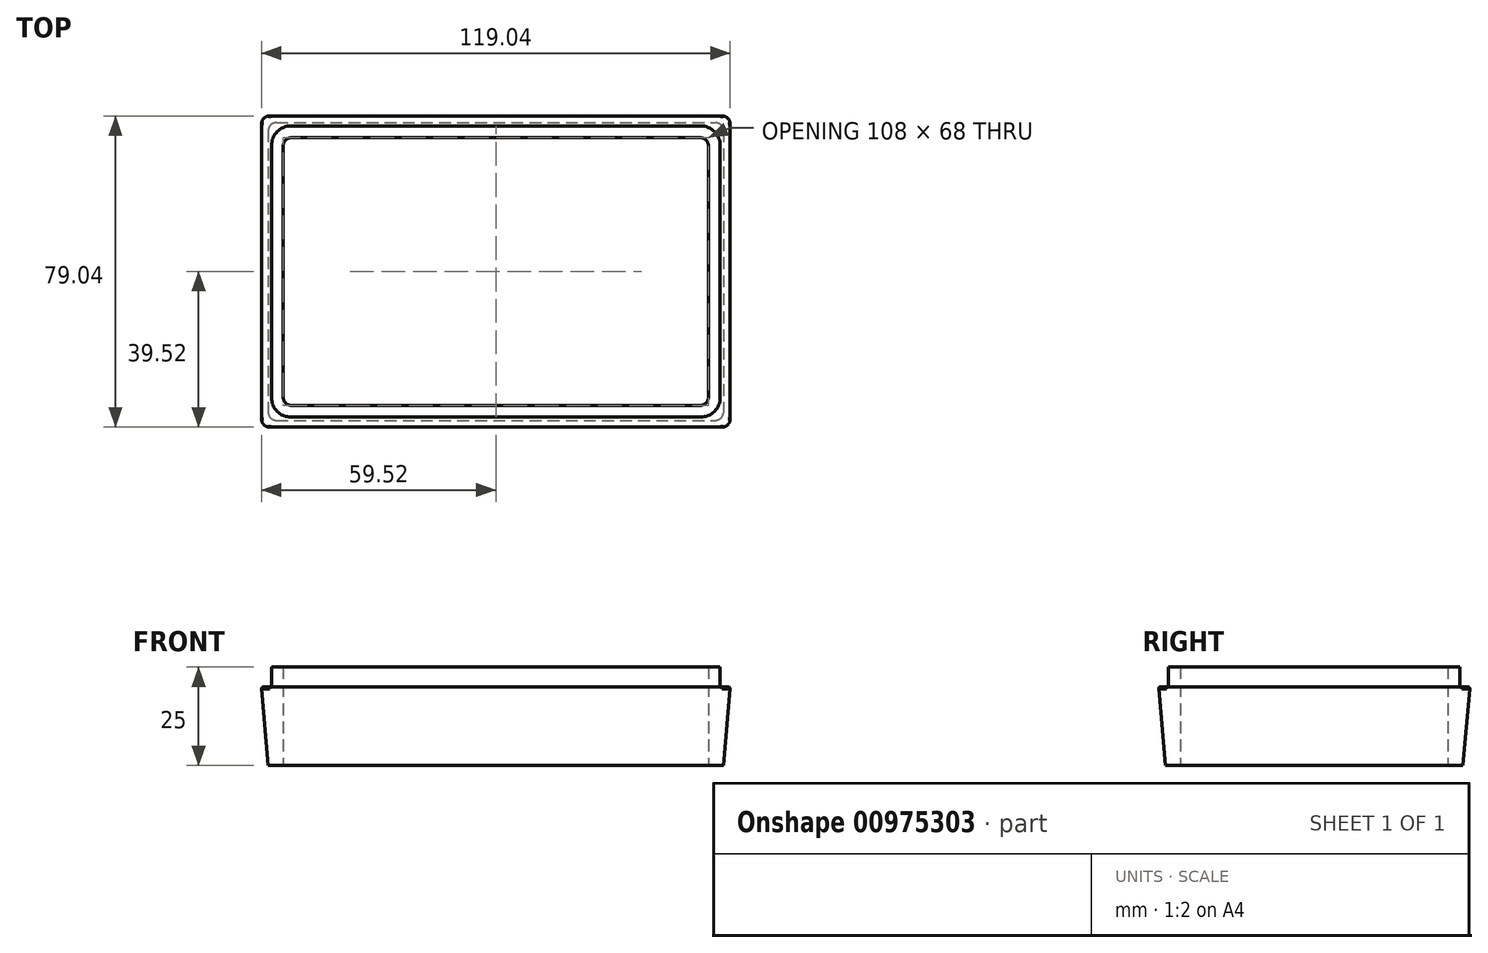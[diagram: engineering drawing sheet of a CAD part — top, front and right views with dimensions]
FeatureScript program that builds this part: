
annotation { "Feature Type Name" : "Feature", "Feature Type Description" : "" }
export const myFeature = defineFeature(function(context is Context, id is Id, definition is map)
    precondition{}
    {
        {
            var Q0;
            Q0=qCreatedBy(makeId("Top.planeOp"),FACE);
            var sketch = newSketch(context, id + "F0", { "sketchPlane" : qUnion([Q0])});
            skLineSegment(sketch, "E0.bottom", {"start": v(-60, 40) * mm, "end": v(60, 40) * mm});
            skLineSegment(sketch, "E0.top", {"start": v(-60, -40) * mm, "end": v(60, -40) * mm});
            skLineSegment(sketch, "E0.left", {"start": v(-60, 40) * mm, "end": v(-60, -40) * mm});
            skLineSegment(sketch, "E0.right", {"start": v(60, 40) * mm, "end": v(60, -40) * mm});
            skLineSegment(sketch, "E1.bottom", {"start": v(-54, 34) * mm, "end": v(54, 34) * mm});
            skLineSegment(sketch, "E1.top", {"start": v(-54, -34) * mm, "end": v(54, -34) * mm});
            skLineSegment(sketch, "E1.left", {"start": v(-54, 34) * mm, "end": v(-54, -34) * mm});
            skLineSegment(sketch, "E1.right", {"start": v(54, 34) * mm, "end": v(54, -34) * mm});
            skSolve(sketch);
        }
        {
            var Q0;
            Q0 = qSketchRegion(id + "F0", true);
            extrude(context, id + "F1", {"entities" : qUnion([Q0]), "depth" : 25 * mm, "offsetDistance" : 25 * mm});
        }
        {
            var Q0;
            Q0=makeQuery(id+"F1.opExtrude","SWEPT_FACE",FACE,{"disambiguationData":[OSD([sQuery(id+"F0.wireOp",EDGE,"E0.top")])]});
            var sketch = newSketch(context, id + "F2", { "sketchPlane" : qUnion([Q0])});
            skLineSegment(sketch, "E2", {"start": v(-60, 25) * mm, "end": v(-57.81, 0) * mm});
            skLineSegment(sketch, "E3", {"start": v(-57.81, 0) * mm, "end": v(57.81, 0) * mm});
            skLineSegment(sketch, "E4", {"start": v(57.81, 0) * mm, "end": v(60, 25) * mm});
            skLineSegment(sketch, "E5", {"start": v(60, 25) * mm, "end": v(75, 25) * mm});
            skLineSegment(sketch, "E6", {"start": v(75, 25) * mm, "end": v(75, -19.68) * mm});
            skLineSegment(sketch, "E7", {"start": v(75, -19.68) * mm, "end": v(-75, -19.68) * mm});
            skLineSegment(sketch, "E8", {"start": v(-75, -19.68) * mm, "end": v(-75, 25) * mm});
            skLineSegment(sketch, "E9", {"start": v(-75, 25) * mm, "end": v(-60, 25) * mm});
            skSolve(sketch);
        }
        {
            var Q0;
            Q0 = qSketchRegion(id + "F2", true);
            extrude(context, id + "F3", {"entities" : qUnion([Q0]), "operationType" : NewBodyOperationType.REMOVE, "endBound" : BoundingType.THROUGH_ALL, "oppositeDirection" : true, "depth" : 25 * mm, "offsetDistance" : 25 * mm});
        }
        {
            var Q0;
            Q0=qCreatedBy(makeId("Right.planeOp"),FACE);
            var sketch = newSketch(context, id + "F4", { "sketchPlane" : qUnion([Q0])});
            skLineSegment(sketch, "E10", {"start": v(40, 25) * mm, "end": v(37.81, 0) * mm});
            skLineSegment(sketch, "E11", {"start": v(37.81, 0) * mm, "end": v(-37.81, 0) * mm});
            skLineSegment(sketch, "E12", {"start": v(-37.81, 0) * mm, "end": v(-40, 25) * mm});
            skLineSegment(sketch, "E13", {"start": v(-40, 25) * mm, "end": v(-55, 25) * mm});
            skLineSegment(sketch, "E14", {"start": v(-55, 25) * mm, "end": v(-55, -15) * mm});
            skLineSegment(sketch, "E15", {"start": v(-55, -15) * mm, "end": v(55, -15) * mm});
            skLineSegment(sketch, "E16", {"start": v(55, -15) * mm, "end": v(55, 25) * mm});
            skLineSegment(sketch, "E17", {"start": v(55, 25) * mm, "end": v(40, 25) * mm});
            skSolve(sketch);
        }
        {
            var Q0;
            Q0 = qSketchRegion(id + "F4", true);
            extrude(context, id + "F5", {"entities" : qUnion([Q0]), "operationType" : NewBodyOperationType.REMOVE, "endBound" : BoundingType.THROUGH_ALL, "oppositeDirection" : true, "depth" : 25 * mm, "offsetDistance" : 25 * mm, "hasSecondDirection" : true, "secondDirectionBound" : SecondDirectionBoundingType.THROUGH_ALL, "secondDirectionOppositeDirection" : false, "secondDirectionDepth" : 25 * mm});
        }
        {
            var Q0;
            Q0=makeQuery(id+"F1.opExtrude","CAP_FACE",FACE,{"disambiguationData":[OSD([sQuery(id+"F0.wireOp",EDGE,"E0.bottom"),sQuery(id+"F0.wireOp",EDGE,"E0.top"),sQuery(id+"F0.wireOp",EDGE,"E0.left"),sQuery(id+"F0.wireOp",EDGE,"E0.right"),sQuery(id+"F0.wireOp",EDGE,"E1.bottom"),sQuery(id+"F0.wireOp",EDGE,"E1.top"),sQuery(id+"F0.wireOp",EDGE,"E1.left"),sQuery(id+"F0.wireOp",EDGE,"E1.right")])],"isStart":false});
            var sketch = newSketch(context, id + "F6", { "sketchPlane" : qUnion([Q0])});
            skLineSegment(sketch, "E18.bottom", {"start": v(-60, 40) * mm, "end": v(60, 40) * mm});
            skLineSegment(sketch, "E18.top", {"start": v(-60, -40) * mm, "end": v(60, -40) * mm});
            skLineSegment(sketch, "E18.left", {"start": v(-60, 40) * mm, "end": v(-60, -40) * mm});
            skLineSegment(sketch, "E18.right", {"start": v(60, 40) * mm, "end": v(60, -40) * mm});
            skLineSegment(sketch, "E19.bottom", {"start": v(-57, 37) * mm, "end": v(57, 37) * mm});
            skLineSegment(sketch, "E19.top", {"start": v(-57, -37) * mm, "end": v(57, -37) * mm});
            skLineSegment(sketch, "E19.left", {"start": v(-57, 37) * mm, "end": v(-57, -37) * mm});
            skLineSegment(sketch, "E19.right", {"start": v(57, 37) * mm, "end": v(57, -37) * mm});
            skSolve(sketch);
        }
        {
            var Q0;
            Q0 = qSketchRegion(id + "F6", true);
            extrude(context, id + "F7", {"entities" : qUnion([Q0]), "operationType" : NewBodyOperationType.REMOVE, "oppositeDirection" : true, "depth" : 5 * mm, "offsetDistance" : 25 * mm});
        }
        {
            var Q0;
            Q0=makeQuery(id+"F7.boolean.opBoolean","COPY",EDGE,{"derivedFrom":makeQuery(id+"F7.opExtrude","SWEPT_EDGE",EDGE,{"disambiguationData":[OSD([sQuery(id+"F6.wireOp",EDGE,"E19.top"),sQuery(id+"F6.wireOp",EDGE,"E19.left")])]})});
            var Q1;
            Q1=makeQuery(id+"F7.boolean.opBoolean","COPY",EDGE,{"derivedFrom":makeQuery(id+"F7.opExtrude","SWEPT_EDGE",EDGE,{"disambiguationData":[OSD([sQuery(id+"F6.wireOp",EDGE,"E19.bottom"),sQuery(id+"F6.wireOp",EDGE,"E19.left")])]})});
            var Q2;
            Q2=makeQuery(id+"F7.boolean.opBoolean","COPY",EDGE,{"derivedFrom":makeQuery(id+"F7.opExtrude","SWEPT_EDGE",EDGE,{"disambiguationData":[OSD([sQuery(id+"F6.wireOp",EDGE,"E19.top"),sQuery(id+"F6.wireOp",EDGE,"E19.right")])]})});
            var Q3;
            Q3=makeQuery(id+"F7.boolean.opBoolean","COPY",EDGE,{"derivedFrom":makeQuery(id+"F7.opExtrude","SWEPT_EDGE",EDGE,{"disambiguationData":[OSD([sQuery(id+"F6.wireOp",EDGE,"E19.bottom"),sQuery(id+"F6.wireOp",EDGE,"E19.right")])]})});
            fillet(context, id + "F8", {"entities" : qUnion([Q0, Q1, Q2, Q3]), "radius" : 5 * mm, "tangentPropagation" : true, "allowEdgeOverflow" : false});
        }
        {
            var Q0;
            Q0=makeQuery(id+"F5.boolean.opBoolean","INTERSECT",EDGE,{"derivedFrom":[makeQuery(id+"F3.boolean.opBoolean","COPY",FACE,{"derivedFrom":makeQuery(id+"F3.opExtrude","SWEPT_FACE",FACE,{"disambiguationData":[OSD([sQuery(id+"F2.wireOp",EDGE,"E2")])]})}),makeQuery(id+"F5.opExtrude","SWEPT_FACE",FACE,{"disambiguationData":[OSD([sQuery(id+"F4.wireOp",EDGE,"E12")])]})]});
            var Q1;
            Q1=makeQuery(id+"F5.boolean.opBoolean","INTERSECT",EDGE,{"derivedFrom":[makeQuery(id+"F3.boolean.opBoolean","COPY",FACE,{"derivedFrom":makeQuery(id+"F3.opExtrude","SWEPT_FACE",FACE,{"disambiguationData":[OSD([sQuery(id+"F2.wireOp",EDGE,"E2")])]})}),makeQuery(id+"F5.opExtrude","SWEPT_FACE",FACE,{"disambiguationData":[OSD([sQuery(id+"F4.wireOp",EDGE,"E10")])]})]});
            var Q2;
            Q2=makeQuery(id+"F5.boolean.opBoolean","INTERSECT",EDGE,{"derivedFrom":[makeQuery(id+"F3.boolean.opBoolean","COPY",FACE,{"derivedFrom":makeQuery(id+"F3.opExtrude","SWEPT_FACE",FACE,{"disambiguationData":[OSD([sQuery(id+"F2.wireOp",EDGE,"E4")])]})}),makeQuery(id+"F5.opExtrude","SWEPT_FACE",FACE,{"disambiguationData":[OSD([sQuery(id+"F4.wireOp",EDGE,"E12")])]})]});
            var Q3;
            Q3=makeQuery(id+"F5.boolean.opBoolean","INTERSECT",EDGE,{"derivedFrom":[makeQuery(id+"F3.boolean.opBoolean","COPY",FACE,{"derivedFrom":makeQuery(id+"F3.opExtrude","SWEPT_FACE",FACE,{"disambiguationData":[OSD([sQuery(id+"F2.wireOp",EDGE,"E4")])]})}),makeQuery(id+"F5.opExtrude","SWEPT_FACE",FACE,{"disambiguationData":[OSD([sQuery(id+"F4.wireOp",EDGE,"E10")])]})]});
            fillet(context, id + "F9", {"entities" : qUnion([Q0, Q1, Q2, Q3]), "radius" : 2 * mm, "tangentPropagation" : true, "allowEdgeOverflow" : false});
        }
        {
            var Q0;
            Q0=makeQuery(id+"F7.boolean.opBoolean","INTERSECT",EDGE,{"derivedFrom":[makeQuery(id+"F5.boolean.opBoolean","COPY",FACE,{"derivedFrom":makeQuery(id+"F5.opExtrude","SWEPT_FACE",FACE,{"disambiguationData":[OSD([sQuery(id+"F4.wireOp",EDGE,"E12")])]})}),makeQuery(id+"F7.opExtrude","CAP_FACE",FACE,{"disambiguationData":[OSD([sQuery(id+"F6.wireOp",EDGE,"E18.bottom"),sQuery(id+"F6.wireOp",EDGE,"E18.top"),sQuery(id+"F6.wireOp",EDGE,"E18.left"),sQuery(id+"F6.wireOp",EDGE,"E18.right"),sQuery(id+"F6.wireOp",EDGE,"E19.bottom"),sQuery(id+"F6.wireOp",EDGE,"E19.top"),sQuery(id+"F6.wireOp",EDGE,"E19.left"),sQuery(id+"F6.wireOp",EDGE,"E19.right")])],"isStart":false})]});
            fillet(context, id + "F10", {"entities" : qUnion([Q0]), "radius" : 0.5 * mm, "tangentPropagation" : true, "allowEdgeOverflow" : false});
        }
        {
            var Q0;
            Q0=makeQuery(id+"F1.opExtrude","SWEPT_EDGE",EDGE,{"disambiguationData":[OSD([sQuery(id+"F0.wireOp",EDGE,"E1.bottom"),sQuery(id+"F0.wireOp",EDGE,"E1.left")])]});
            var Q1;
            Q1=makeQuery(id+"F1.opExtrude","SWEPT_EDGE",EDGE,{"disambiguationData":[OSD([sQuery(id+"F0.wireOp",EDGE,"E1.top"),sQuery(id+"F0.wireOp",EDGE,"E1.left")])]});
            var Q2;
            Q2=makeQuery(id+"F1.opExtrude","SWEPT_EDGE",EDGE,{"disambiguationData":[OSD([sQuery(id+"F0.wireOp",EDGE,"E1.top"),sQuery(id+"F0.wireOp",EDGE,"E1.right")])]});
            var Q3;
            Q3=makeQuery(id+"F1.opExtrude","SWEPT_EDGE",EDGE,{"disambiguationData":[OSD([sQuery(id+"F0.wireOp",EDGE,"E1.bottom"),sQuery(id+"F0.wireOp",EDGE,"E1.right")])]});
            fillet(context, id + "F11", {"entities" : qUnion([Q0, Q1, Q2, Q3]), "radius" : 2 * mm, "tangentPropagation" : true, "allowEdgeOverflow" : false});
        }
    });
